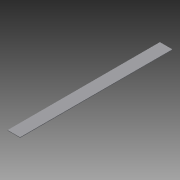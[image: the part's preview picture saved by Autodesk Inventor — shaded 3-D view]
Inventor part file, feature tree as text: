
AUTODESK INVENTOR PART (.ipt)
format: ipt  version: 2015 SP1 (Build 190203100, 203)  size: 68,608 bytes
history: native  units: mm
features: extrude x1, sketch x1
ambient origin geometry x8: Origin, YZ Plane, XZ Plane, XY Plane, X Axis, Y Axis, Z Axis, Center Point
bodies: Solid1 (feature_tree)
feature tree (2):
  extrude  "Extrusion1"  Depth=8.0mm
  sketch  "Sketch1"  dims[d0=176.0mm d1=8.0mm d2=2150.0mm d3=0.0mm]
